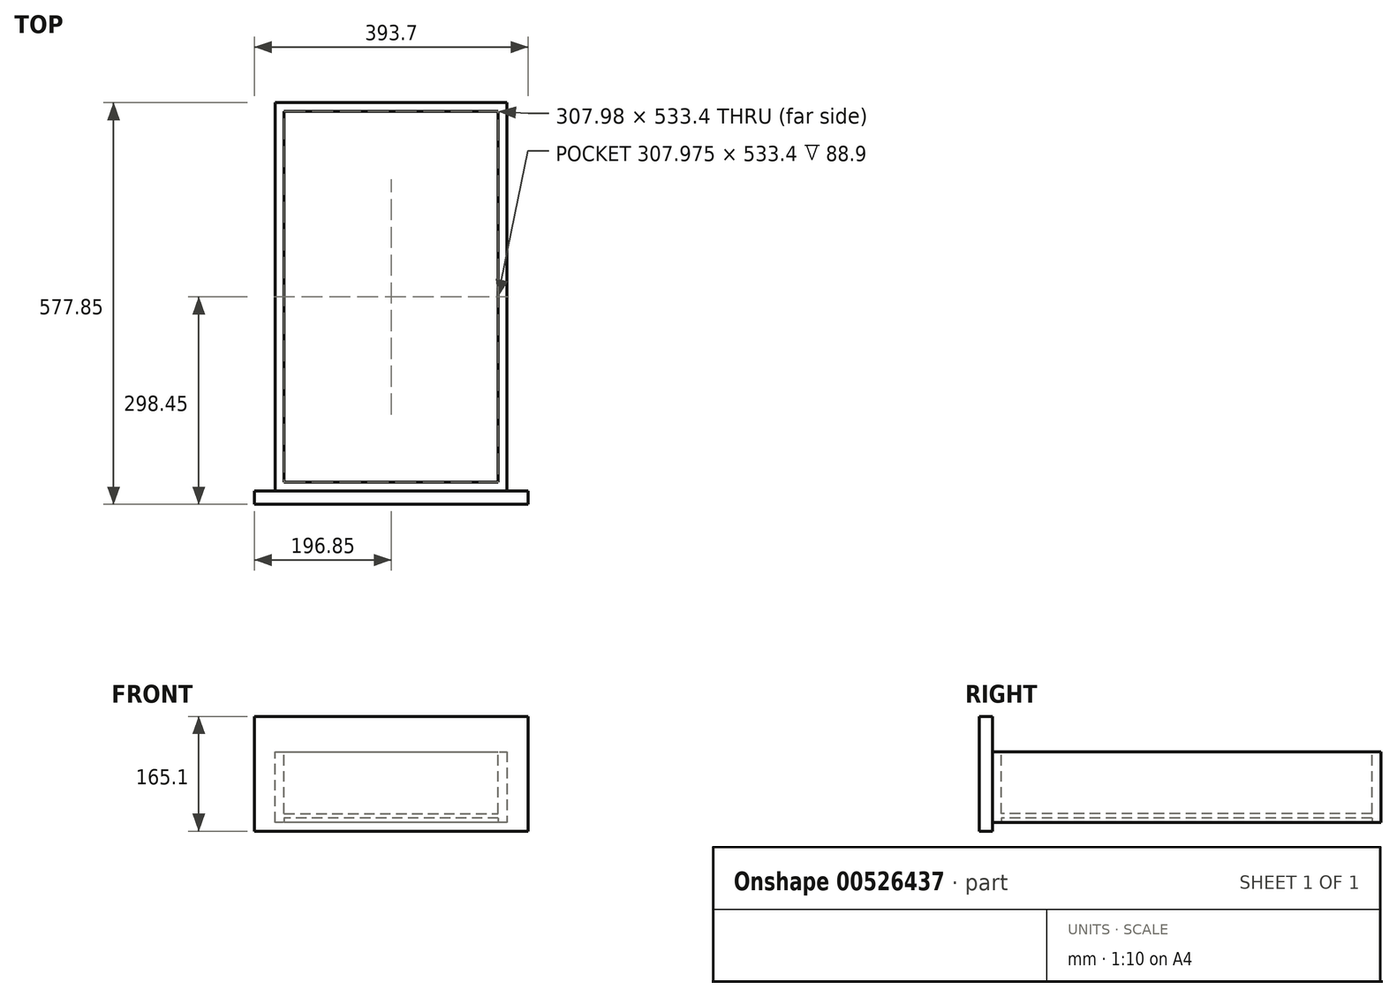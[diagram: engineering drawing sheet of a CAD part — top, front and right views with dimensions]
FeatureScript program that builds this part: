
annotation { "Feature Type Name" : "Feature", "Feature Type Description" : "" }
export const myFeature = defineFeature(function(context is Context, id is Id, definition is map)
    precondition{}
    {
        {
            var Q0;
            Q0=qCreatedBy(makeId("Front.planeOp"),FACE);
            var sketch = newSketch(context, id + "F0", { "sketchPlane" : qUnion([Q0])});
            skLineSegment(sketch, "E0.bottom", {"start": v(196.85, 82.55) * mm, "end": v(-196.85, 82.55) * mm});
            skLineSegment(sketch, "E0.top", {"start": v(196.85, -82.55) * mm, "end": v(-196.85, -82.55) * mm});
            skLineSegment(sketch, "E0.left", {"start": v(196.85, 82.55) * mm, "end": v(196.85, -82.55) * mm});
            skLineSegment(sketch, "E0.right", {"start": v(-196.85, 82.55) * mm, "end": v(-196.85, -82.55) * mm});
            skPoint(sketch, "E0.middle", {"position": v(0, 0) * mm});
            skSolve(sketch);
        }
        {
            var Q0;
            Q0=makeQuery(id+"F0.imprint","IMPRINT",FACE,{"disambiguationData":[TD([[makeQuery(id+"F0.imprint","IMPRINT",EDGE,{"derivedFrom":sQuery(id+"F0.wireOp",EDGE,"E0.bottom")}),1.0]])]});
            extrude(context, id + "F1", {"entities" : qUnion([Q0]), "depth" : 19.05 * mm, "offsetDistance" : 25.4 * mm});
        }
        {
            var Q0;
            Q0=makeQuery(id+"F1.opExtrude","CAP_FACE",FACE,{"disambiguationData":[OSD([sQuery(id+"F0.wireOp",EDGE,"E0.bottom"),sQuery(id+"F0.wireOp",EDGE,"E0.top"),sQuery(id+"F0.wireOp",EDGE,"E0.left"),sQuery(id+"F0.wireOp",EDGE,"E0.right")])],"isStart":true});
            var sketch = newSketch(context, id + "F2", { "sketchPlane" : qUnion([Q0])});
            skLineSegment(sketch, "E1", {"start": v(0, -82.55) * mm, "end": v(0, -69.85) * mm});
            skPoint(sketch, "E1.endSnap0", {"position": v(0, -82.55) * mm});
            skLineSegment(sketch, "E2", {"start": v(0, -69.85) * mm, "end": v(166.69, -69.85) * mm});
            skLineSegment(sketch, "E3", {"start": v(166.69, -69.85) * mm, "end": v(166.69, 31.75) * mm});
            skLineSegment(sketch, "E4", {"start": v(166.69, 31.75) * mm, "end": v(-166.69, 31.75) * mm});
            skLineSegment(sketch, "E5", {"start": v(-166.69, 31.75) * mm, "end": v(-166.69, -69.85) * mm});
            skLineSegment(sketch, "E6", {"start": v(-166.69, -69.85) * mm, "end": v(0, -69.85) * mm});
            skSolve(sketch);
        }
        {
            var Q0;
            Q0=makeQuery(id+"F2.imprint","IMPRINT",FACE,{"disambiguationData":[TD([[makeQuery(id+"F2.imprint","IMPRINT",EDGE,{"derivedFrom":sQuery(id+"F2.wireOp",EDGE,"E2")}),1.0]])]});
            extrude(context, id + "F3", {"entities" : qUnion([Q0]), "operationType" : NewBodyOperationType.ADD, "depth" : 558.8 * mm, "offsetDistance" : 25.4 * mm});
        }
        {
            var Q0;
            Q0=makeQuery(id+"F3.opExtrude","SWEPT_FACE",FACE,{"disambiguationData":[OSD([sQuery(id+"F2.wireOp",EDGE,"E4")])]});
            var sketch = newSketch(context, id + "F4", { "sketchPlane" : qUnion([Q0])});
            skLineSegment(sketch, "E7", {"start": v(-166.69, 558.8) * mm, "end": v(-153.99, 558.8) * mm});
            skLineSegment(sketch, "E8", {"start": v(-153.99, 558.8) * mm, "end": v(-153.99, 546.1) * mm});
            skLineSegment(sketch, "E9.bottom", {"start": v(-153.99, 546.1) * mm, "end": v(153.99, 546.1) * mm});
            skLineSegment(sketch, "E9.top", {"start": v(-153.99, 12.7) * mm, "end": v(153.99, 12.7) * mm});
            skLineSegment(sketch, "E9.left", {"start": v(-153.99, 546.1) * mm, "end": v(-153.99, 12.7) * mm});
            skLineSegment(sketch, "E9.right", {"start": v(153.99, 546.1) * mm, "end": v(153.99, 12.7) * mm});
            skSolve(sketch);
        }
        {
            var Q0;
            Q0=makeQuery(id+"F4.imprint","IMPRINT",FACE,{"disambiguationData":[TD([[makeQuery(id+"F4.imprint","IMPRINT",EDGE,{"derivedFrom":sQuery(id+"F4.wireOp",EDGE,"E9.bottom")}),-1.0]])]});
            extrude(context, id + "F5", {"entities" : qUnion([Q0]), "operationType" : NewBodyOperationType.REMOVE, "oppositeDirection" : true, "depth" : 88.9 * mm, "offsetDistance" : 25.4 * mm});
        }
        {
            var Q0;
            Q0=makeQuery(id+"F3.opExtrude","SWEPT_FACE",FACE,{"disambiguationData":[OSD([sQuery(id+"F2.wireOp",EDGE,"E2"),sQuery(id+"F2.wireOp",EDGE,"E6")])]});
            var sketch = newSketch(context, id + "F6", { "sketchPlane" : qUnion([Q0])});
            skLineSegment(sketch, "E10", {"start": v(166.69, -558.8) * mm, "end": v(153.99, -558.8) * mm});
            skLineSegment(sketch, "E11", {"start": v(153.99, -558.8) * mm, "end": v(153.99, -546.1) * mm});
            skLineSegment(sketch, "E12.bottom", {"start": v(153.99, -546.1) * mm, "end": v(-153.99, -546.1) * mm});
            skLineSegment(sketch, "E12.top", {"start": v(153.99, -12.7) * mm, "end": v(-153.99, -12.7) * mm});
            skLineSegment(sketch, "E12.left", {"start": v(153.99, -546.1) * mm, "end": v(153.99, -12.7) * mm});
            skLineSegment(sketch, "E12.right", {"start": v(-153.99, -546.1) * mm, "end": v(-153.99, -12.7) * mm});
            skSolve(sketch);
        }
        {
            var Q0;
            Q0=makeQuery(id+"F6.imprint","IMPRINT",FACE,{"disambiguationData":[TD([[makeQuery(id+"F6.imprint","IMPRINT",EDGE,{"derivedFrom":sQuery(id+"F6.wireOp",EDGE,"E12.bottom")}),-1.0]])]});
            extrude(context, id + "F7", {"entities" : qUnion([Q0]), "operationType" : NewBodyOperationType.REMOVE, "oppositeDirection" : true, "depth" : 6.35 * mm, "offsetDistance" : 25.4 * mm});
        }
    });
